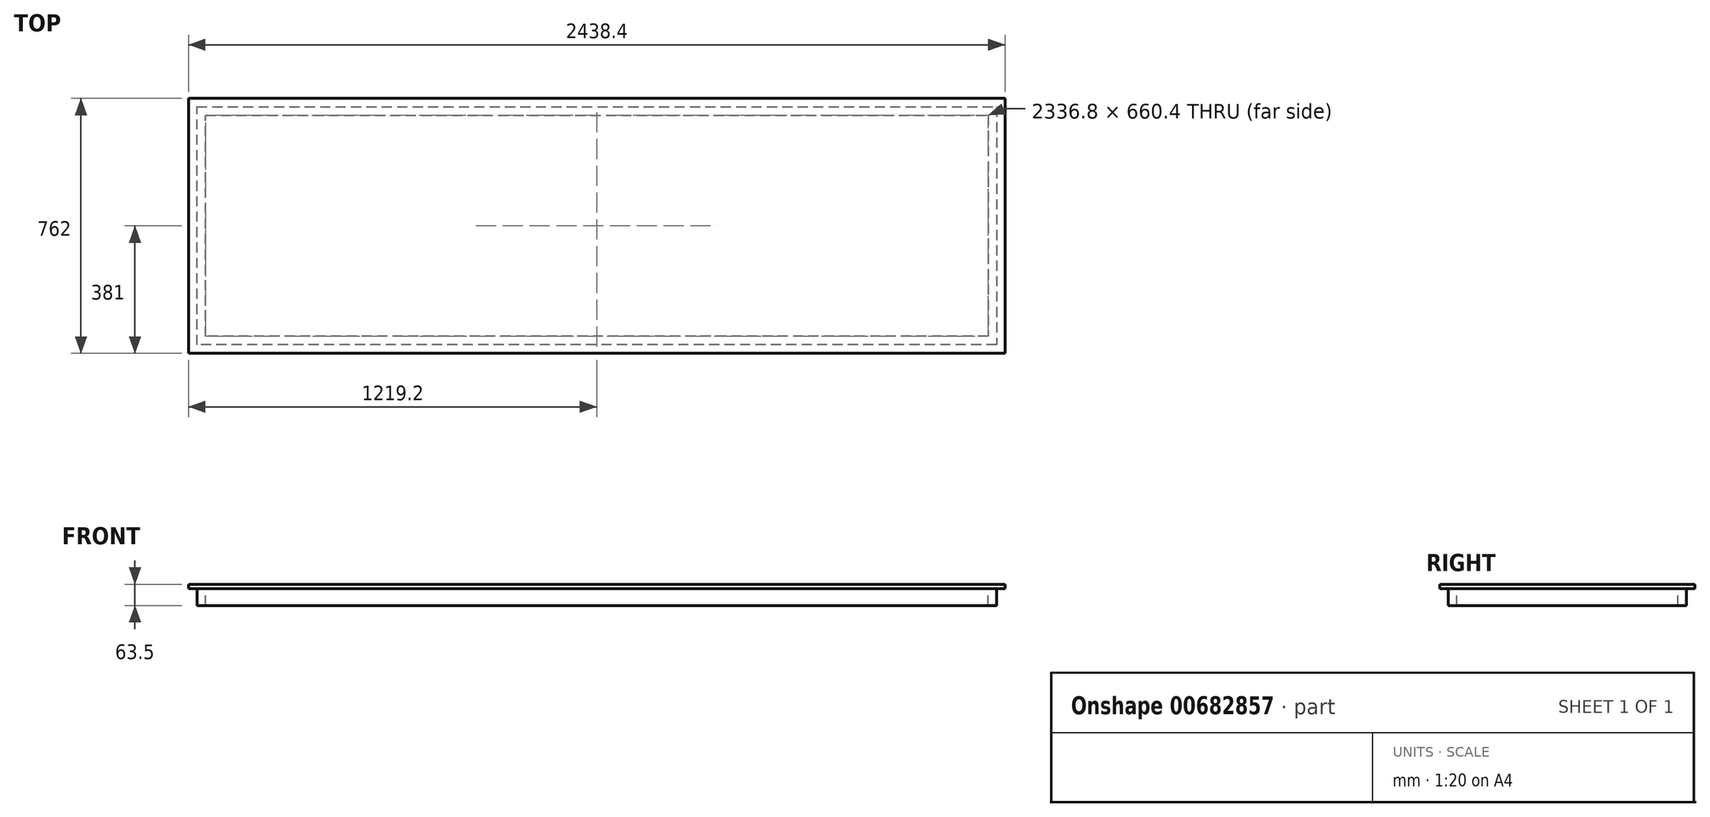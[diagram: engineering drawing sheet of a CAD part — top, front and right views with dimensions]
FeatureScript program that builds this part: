
annotation { "Feature Type Name" : "Feature", "Feature Type Description" : "" }
export const myFeature = defineFeature(function(context is Context, id is Id, definition is map)
    precondition{}
    {
        {
            var Q0;
            Q0=qCreatedBy(makeId("Top.planeOp"),FACE);
            var sketch = newSketch(context, id + "F0", { "sketchPlane" : qUnion([Q0])});
            skLineSegment(sketch, "E0.bottom", {"start": v(1219.2, 381) * mm, "end": v(-1219.2, 381) * mm});
            skLineSegment(sketch, "E0.top", {"start": v(1219.2, -381) * mm, "end": v(-1219.2, -381) * mm});
            skLineSegment(sketch, "E0.left", {"start": v(1219.2, 381) * mm, "end": v(1219.2, -381) * mm});
            skLineSegment(sketch, "E0.right", {"start": v(-1219.2, 381) * mm, "end": v(-1219.2, -381) * mm});
            skPoint(sketch, "E0.middle", {"position": v(0, 0) * mm});
            skSolve(sketch);
        }
        {
            var Q0;
            Q0=qCreatedBy(makeId("Front.planeOp"),FACE);
            var sketch = newSketch(context, id + "F1", { "sketchPlane" : qUnion([Q0])});
            skLineSegment(sketch, "E1.bottom", {"start": v(1168.4, -50.8) * mm, "end": v(1193.8, -50.8) * mm});
            skLineSegment(sketch, "E1.top", {"start": v(1168.4, 0) * mm, "end": v(1193.8, 0) * mm});
            skLineSegment(sketch, "E1.left", {"start": v(1168.4, -50.8) * mm, "end": v(1168.4, 0) * mm});
            skLineSegment(sketch, "E1.right", {"start": v(1193.8, -50.8) * mm, "end": v(1193.8, 0) * mm});
            skPoint(sketch, "E1.middle", {"position": v(1181.1, -25.4) * mm});
            skSolve(sketch);
        }
        {
            var Q0;
            Q0=makeQuery(id+"F1.imprint","IMPRINT",FACE,{"disambiguationData":[TD([[makeQuery(id+"F1.imprint","IMPRINT",EDGE,{"derivedFrom":sQuery(id+"F1.wireOp",EDGE,"E1.bottom")}),1.0]])]});
            var Q1;
            Q1=sQuery(id+"F0.wireOp",EDGE,"E0.left");
            var Q2;
            Q2=sQuery(id+"F0.wireOp",EDGE,"E0.bottom");
            var Q3;
            Q3=sQuery(id+"F0.wireOp",EDGE,"E0.right");
            var Q4;
            Q4=sQuery(id+"F0.wireOp",EDGE,"E0.top");
            sweep(context, id + "F2", {"profiles" : qUnion([Q0]), "path" : qUnion([Q1, Q2, Q3, Q4])});
        }
        {
            var Q0;
            Q0 = qSketchRegion(id + "F0", true);
            extrude(context, id + "F3", {"entities" : qUnion([Q0]), "depth" : 12.7 * mm, "offsetDistance" : 25.4 * mm});
        }
    });
